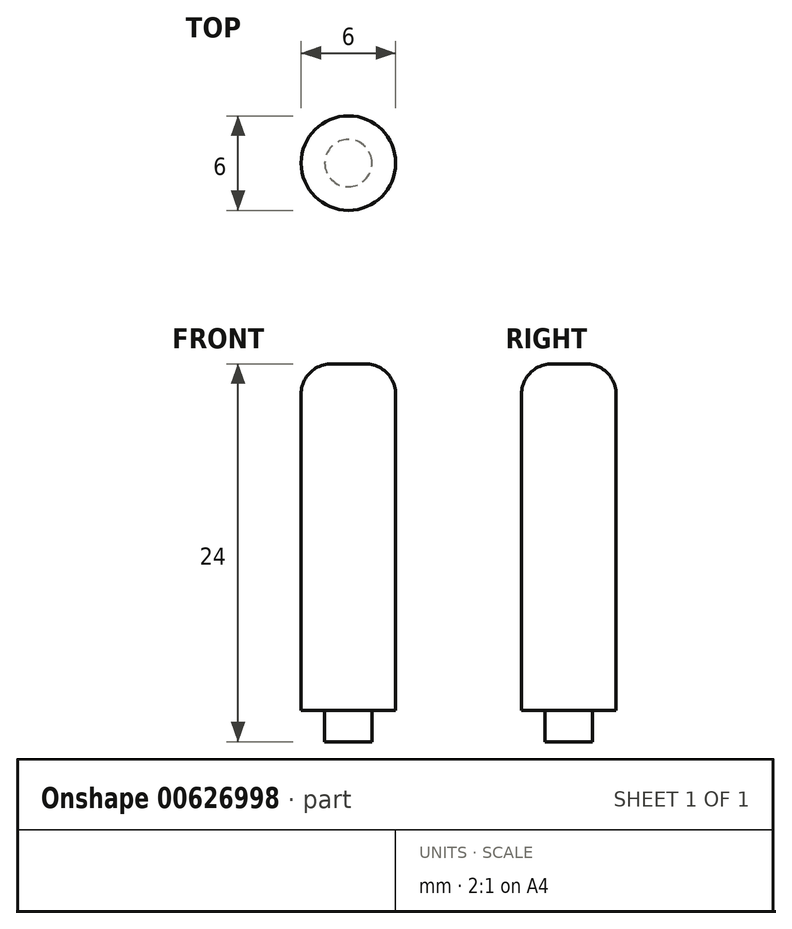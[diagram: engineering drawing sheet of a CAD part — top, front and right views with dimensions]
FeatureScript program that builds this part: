
annotation { "Feature Type Name" : "Feature", "Feature Type Description" : "" }
export const myFeature = defineFeature(function(context is Context, id is Id, definition is map)
    precondition{}
    {
        {
            var Q0;
            Q0=qCreatedBy(makeId("Top.planeOp"),FACE);
            var sketch = newSketch(context, id + "F0", { "sketchPlane" : qUnion([Q0])});
            skCircle(sketch, "E0", {"center": v(0, 0) * mm, "radius": 3 * mm});
            skSolve(sketch);
        }
        {
            var Q0;
            Q0=makeQuery(id+"F0.imprint","IMPRINT",FACE,{"disambiguationData":[TD([[makeQuery(id+"F0.imprint","IMPRINT",EDGE,{"derivedFrom":sQuery(id+"F0.wireOp",EDGE,"E0")}),1.0]])]});
            extrude(context, id + "F1", {"entities" : qUnion([Q0]), "depth" : 22 * mm, "offsetDistance" : 25 * mm});
        }
        {
            var Q0;
            Q0=makeQuery(id+"F1.opExtrude","CAP_EDGE",EDGE,{"disambiguationData":[OSD([sQuery(id+"F0.wireOp",EDGE,"E0")])],"isStart":false});
            fillet(context, id + "F2", {"entities" : qUnion([Q0]), "radius" : 1.93 * mm, "tangentPropagation" : true, "allowEdgeOverflow" : false});
        }
        {
            var Q0;
            Q0=makeQuery(id+"F1.opExtrude","CAP_FACE",FACE,{"disambiguationData":[OSD([sQuery(id+"F0.wireOp",EDGE,"E0")])],"isStart":true});
            var sketch = newSketch(context, id + "F3", { "sketchPlane" : qUnion([Q0])});
            skCircle(sketch, "E1", {"center": v(0, 0) * mm, "radius": 1.5 * mm});
            skSolve(sketch);
        }
        {
            var Q0;
            Q0=makeQuery(id+"F3.imprint","IMPRINT",FACE,{"disambiguationData":[TD([[makeQuery(id+"F3.imprint","IMPRINT",EDGE,{"derivedFrom":sQuery(id+"F3.wireOp",EDGE,"E1")}),1.0]])]});
            extrude(context, id + "F4", {"entities" : qUnion([Q0]), "operationType" : NewBodyOperationType.ADD, "depth" : 2 * mm, "offsetDistance" : 25 * mm});
        }
    });
